# Revit family: LF6LED
name_source: partatom
category: Lighting Fixtures
revit_build: Autodesk Revit 2014 (Build: 20130308_1515(x64)
units: mm (PartAtom-declared; Revit-internal decimal feet)

## types (1)
- LF6
    Apparent Load = 0 VA
    Assembly Code = D5020200
    Backbox = Paint-Hubbell-White
    Color Filter = 16777215
    Default Elevation = 48.000"
    Description = 6'' architectural LED downlight with color consistency from fixture to fixture
    Dimming Lamp Color Temperature Shift = <None>
    Emit Shape Visible in Rendering = No
    Emit from Circle Diameter = 5.500"
    Glass = Glass
    Is 120V = Yes
    Is 277V = No
    Lamp = LED
    Load Classification = Lighting
    Manufacturer = Prescolite
    Model = LF6LED
    Mounting = Recessed
    Photometric Notes = More IES files download on Photometric Link
    Photometric Web File = LF6ML-6LFML30L30K8.IES
    Photometric Web Link = https://www.hubbell.com
    Product Documentation Link = https://hubbellcdn.com
    Product Page URL = https://www.hubbell.com
    Steel = Steel
    Tilt Angle = -90.00°
    Type Comments = Lighting Fixture
    URL = https://www.hubbell.com
    Voltage = 120 V
    Warranty = 5-Years Warranty
    Wattage Comments = 19W
    Wire = Wire

## geometry (parser evidence)
native form markers: Blend x1, Sweep x2
no freeform markers — native parametric forms only
